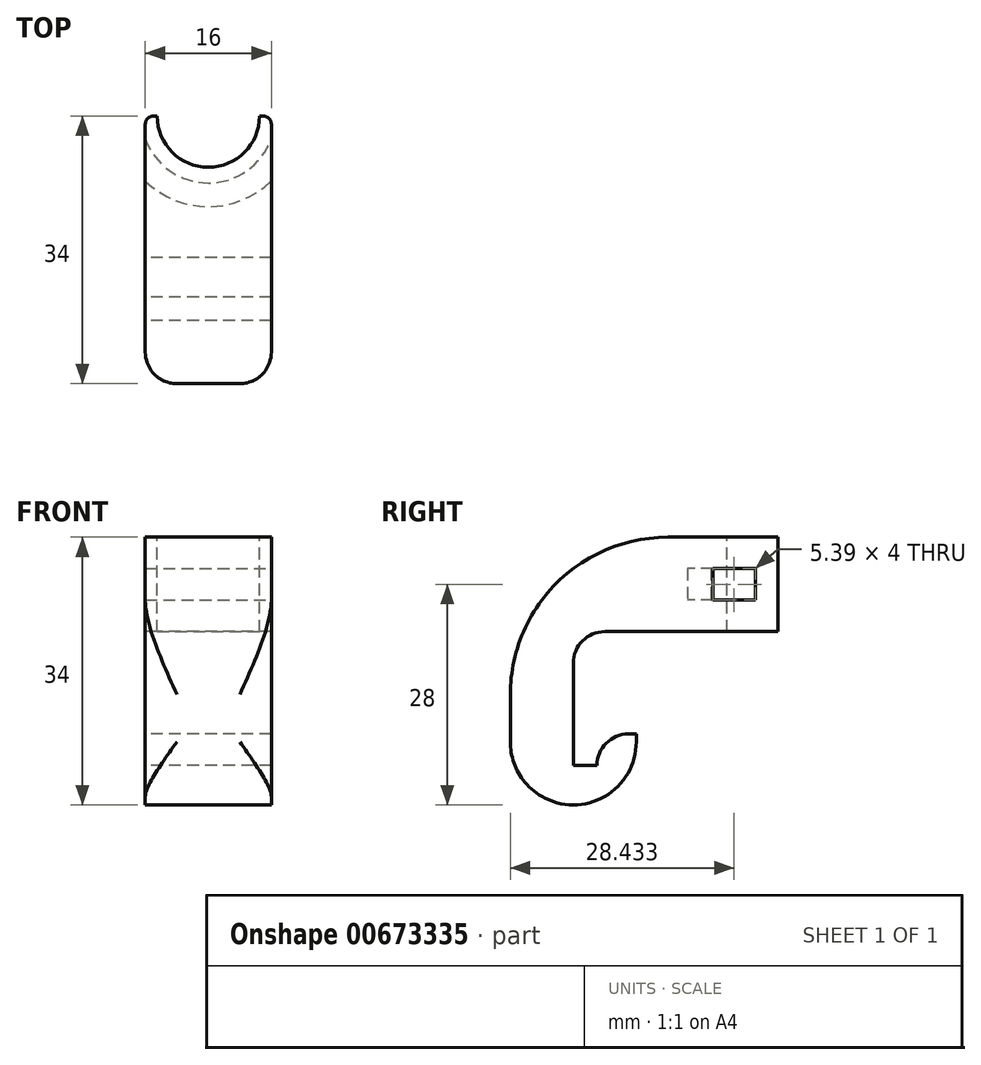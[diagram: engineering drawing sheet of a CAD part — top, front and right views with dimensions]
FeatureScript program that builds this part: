
annotation { "Feature Type Name" : "Feature", "Feature Type Description" : "" }
export const myFeature = defineFeature(function(context is Context, id is Id, definition is map)
    precondition{}
    {
        {
            var Q0;
            Q0=qCreatedBy(makeId("Right.planeOp"),FACE);
            var sketch = newSketch(context, id + "F0", { "sketchPlane" : qUnion([Q0])});
            skLineSegment(sketch, "E0", {"start": v(0, 34) * mm, "end": v(0, 0) * mm});
            skLineSegment(sketch, "E1", {"start": v(0, 0) * mm, "end": v(16, 0) * mm});
            skLineSegment(sketch, "E2", {"start": v(16, 0) * mm, "end": v(16, 9) * mm});
            skLineSegment(sketch, "E3", {"start": v(16, 9) * mm, "end": v(11, 9) * mm});
            skLineSegment(sketch, "E4", {"start": v(11, 9) * mm, "end": v(11, 5) * mm});
            skLineSegment(sketch, "E5", {"start": v(11, 5) * mm, "end": v(8, 5) * mm});
            skLineSegment(sketch, "E6", {"start": v(8, 5) * mm, "end": v(8, 22) * mm});
            skLineSegment(sketch, "E7", {"start": v(8, 22) * mm, "end": v(34, 22) * mm});
            skLineSegment(sketch, "E8", {"start": v(34, 22) * mm, "end": v(34, 34) * mm});
            skLineSegment(sketch, "E9", {"start": v(34, 34) * mm, "end": v(0, 34) * mm});
            skSolve(sketch);
        }
        {
            var Q0;
            Q0=makeQuery(id+"F0.imprint","IMPRINT",FACE,{"disambiguationData":[TD([[makeQuery(id+"F0.imprint","IMPRINT",EDGE,{"derivedFrom":sQuery(id+"F0.wireOp",EDGE,"E0")}),1.0]])]});
            extrude(context, id + "F1", {"entities" : qUnion([Q0]), "depth" : 16 * mm, "offsetDistance" : 25 * mm});
        }
        {
            var Q0;
            Q0=makeQuery(id+"F1.opExtrude","SWEPT_EDGE",EDGE,{"disambiguationData":[OSD([sQuery(id+"F0.wireOp",EDGE,"E1"),sQuery(id+"F0.wireOp",EDGE,"E2")])]});
            var Q1;
            Q1=makeQuery(id+"F1.opExtrude","SWEPT_EDGE",EDGE,{"disambiguationData":[OSD([sQuery(id+"F0.wireOp",EDGE,"E0"),sQuery(id+"F0.wireOp",EDGE,"E1")])]});
            fillet(context, id + "F2", {"entities" : qUnion([Q0, Q1]), "radius" : 8 * mm, "tangentPropagation" : true, "allowEdgeOverflow" : false});
        }
        {
            var Q0;
            Q0=makeQuery(id+"F1.opExtrude","SWEPT_EDGE",EDGE,{"disambiguationData":[OSD([sQuery(id+"F0.wireOp",EDGE,"E0"),sQuery(id+"F0.wireOp",EDGE,"E9")])]});
            fillet(context, id + "F3", {"entities" : qUnion([Q0]), "radius" : 20 * mm, "tangentPropagation" : true, "allowEdgeOverflow" : false});
        }
        {
            var Q0;
            Q0=makeQuery(id+"F1.opExtrude","SWEPT_EDGE",EDGE,{"disambiguationData":[OSD([sQuery(id+"F0.wireOp",EDGE,"E6"),sQuery(id+"F0.wireOp",EDGE,"E7")])]});
            var Q1;
            Q1=makeQuery(id+"F1.opExtrude","SWEPT_EDGE",EDGE,{"disambiguationData":[OSD([sQuery(id+"F0.wireOp",EDGE,"E3"),sQuery(id+"F0.wireOp",EDGE,"E4")])]});
            fillet(context, id + "F4", {"entities" : qUnion([Q0, Q1]), "radius" : 4 * mm, "tangentPropagation" : true, "allowEdgeOverflow" : false});
        }
        {
            var Q0;
            Q0=makeQuery(id+"F1.opExtrude","SWEPT_FACE",FACE,{"disambiguationData":[OSD([sQuery(id+"F0.wireOp",EDGE,"E9")])]});
            var sketch = newSketch(context, id + "F5", { "sketchPlane" : qUnion([Q0])});
            skCircle(sketch, "E10", {"center": v(8, 34) * mm, "radius": 6.5 * mm});
            skSolve(sketch);
        }
        {
            var Q0;
            {var subQ0=sQuery(id+"F5.wireOp",EDGE,"E10");var subQ1=makeQuery(id+"F1.opExtrude","SWEPT_EDGE",EDGE,{"disambiguationData":[OSD([sQuery(id+"F0.wireOp",EDGE,"E8"),sQuery(id+"F0.wireOp",EDGE,"E9")])]});var subQ2=makeQuery(id+"F5.imprint","INTERSECT",VERTEX,{"disambiguationData":[OD(0.0)],"derivedFrom":[subQ1,subQ0]});Q0=makeQuery(id+"F5.imprint","IMPRINT",FACE,{"disambiguationData":[TD([[makeQuery(id+"F5.imprint","IMPRINT",EDGE,{"disambiguationData":[TD([[subQ2,-1.0]])],"derivedFrom":subQ0}),1.0]])]});}
            extrude(context, id + "F6", {"entities" : qUnion([Q0]), "operationType" : NewBodyOperationType.REMOVE, "endBound" : BoundingType.THROUGH_ALL, "oppositeDirection" : true, "depth" : 25 * mm, "offsetDistance" : 25 * mm});
        }
        {
            var Q0;
            Q0=makeQuery(id+"F1.opExtrude","SWEPT_FACE",FACE,{"disambiguationData":[OSD([sQuery(id+"F0.wireOp",EDGE,"E9")])]});
            var sketch = newSketch(context, id + "F7", { "sketchPlane" : qUnion([Q0])});
            skCircle(sketch, "E11", {"center": v(8, 34) * mm, "radius": 8.5 * mm});
            skCircle(sketch, "E12", {"center": v(8, 34) * mm, "radius": 11.5 * mm});
            skSolve(sketch);
        }
        {
            var Q0;
            {var subQ1=sQuery(id+"F0.wireOp",EDGE,"E9");var subQ15=makeQuery(id+"F1.opExtrude","CAP_EDGE",EDGE,{"disambiguationData":[OSD([subQ1])],"isStart":true});var subQ19=sQuery(id+"F7.wireOp",EDGE,"E12");var subQ21=makeQuery(id+"F7.imprint","INTERSECT",VERTEX,{"derivedFrom":[subQ15,subQ19]});Q0=makeQuery(id+"F7.imprint","IMPRINT",FACE,{"disambiguationData":[TD([[makeQuery(id+"F7.imprint","IMPRINT",EDGE,{"disambiguationData":[TD([[subQ21,-1.0]])],"derivedFrom":subQ19}),1.0]])]});}
            extrude(context, id + "F8", {"entities" : qUnion([Q0]), "depth" : 4 * mm, "offsetDistance" : 25 * mm});
        }
        {
            var Q0;
            Q0=makeQuery(id+"F8.opExtrude","SWEPT_BODY",BODY,{"disambiguationData":[OSD([sQuery(id+"F0.wireOp",EDGE,"E9"),sQuery(id+"F7.wireOp",EDGE,"E11"),sQuery(id+"F7.wireOp",EDGE,"E12")])]});
            transform(context, id + "F9", {"entities" : qUnion([Q0]), "transformType" : TransformType.TRANSLATION_3D, "dx" : 0 * mm, "dy" : 0 * mm, "dz" : -8 * mm, "makeCopy" : false});
        }
        {
            var Q0;
            Q0=makeQuery(id+"F8.opExtrude","SWEPT_BODY",BODY,{"disambiguationData":[OSD([sQuery(id+"F0.wireOp",EDGE,"E9"),sQuery(id+"F7.wireOp",EDGE,"E11"),sQuery(id+"F7.wireOp",EDGE,"E12")])]});
            var Q1;
            Q1=makeQuery(id+"F1.opExtrude","SWEPT_BODY",BODY,{"disambiguationData":[OSD([sQuery(id+"F0.wireOp",EDGE,"E0"),sQuery(id+"F0.wireOp",EDGE,"E1"),sQuery(id+"F0.wireOp",EDGE,"E2"),sQuery(id+"F0.wireOp",EDGE,"E3"),sQuery(id+"F0.wireOp",EDGE,"E4"),sQuery(id+"F0.wireOp",EDGE,"E5"),sQuery(id+"F0.wireOp",EDGE,"E6"),sQuery(id+"F0.wireOp",EDGE,"E7"),sQuery(id+"F0.wireOp",EDGE,"E8"),sQuery(id+"F0.wireOp",EDGE,"E9")])]});
            booleanBodies(context, id + "F10", {"operationType" : BooleanOperationType.SUBTRACTION, "tools" : qUnion([Q0]), "targets" : qUnion([Q1])});
        }
        {
            var Q0;
            {var subQ0=sQuery(id+"F7.wireOp",EDGE,"E11");var subQ1=sQuery(id+"F0.wireOp",EDGE,"E9");var subQ2=sQuery(id+"F0.wireOp",EDGE,"E8");Q0=makeQuery(id+"F10.opBoolean","MERGE",EDGE,{"derivedFrom":[makeQuery(id+"F1.opExtrude","CAP_EDGE",EDGE,{"disambiguationData":[OSD([subQ2])],"isStart":false}),makeQuery(id+"F8.opExtrude","SWEPT_EDGE",EDGE,{"disambiguationData":[OSD([subQ2,subQ1,subQ0]),TDD([makeQuery(id+"F7.imprint","INTERSECT",VERTEX,{"derivedFrom":[makeQuery(id+"F1.opExtrude","CAP_EDGE",EDGE,{"disambiguationData":[OSD([subQ1])],"isStart":false}),makeQuery(id+"F6.boolean.opBoolean","SPLIT",EDGE,{"disambiguationData":[TD([makeQuery(id+"F1.opExtrude","CAP_FACE",FACE,{"disambiguationData":[OSD([sQuery(id+"F0.wireOp",EDGE,"E0"),sQuery(id+"F0.wireOp",EDGE,"E1"),sQuery(id+"F0.wireOp",EDGE,"E2"),sQuery(id+"F0.wireOp",EDGE,"E3"),sQuery(id+"F0.wireOp",EDGE,"E4"),sQuery(id+"F0.wireOp",EDGE,"E5"),sQuery(id+"F0.wireOp",EDGE,"E6"),sQuery(id+"F0.wireOp",EDGE,"E7"),subQ2,subQ1])],"isStart":false})])],"derivedFrom":makeQuery(id+"F1.opExtrude","SWEPT_EDGE",EDGE,{"disambiguationData":[OSD([subQ2,subQ1])]})}),subQ0]})])]})]});}
            var Q1;
            {var subQ0=sQuery(id+"F7.wireOp",EDGE,"E12");var subQ1=sQuery(id+"F0.wireOp",EDGE,"E9");Q1=makeQuery(id+"F10.opBoolean","COPY",EDGE,{"derivedFrom":makeQuery(id+"F8.opExtrude","SWEPT_EDGE",EDGE,{"disambiguationData":[OSD([subQ1,subQ0]),TDD([makeQuery(id+"F7.imprint","INTERSECT",VERTEX,{"derivedFrom":[makeQuery(id+"F1.opExtrude","CAP_EDGE",EDGE,{"disambiguationData":[OSD([subQ1])],"isStart":false}),subQ0]})])]})});}
            var Q2;
            {var subQ0=sQuery(id+"F7.wireOp",EDGE,"E11");var subQ1=sQuery(id+"F0.wireOp",EDGE,"E9");var subQ2=sQuery(id+"F0.wireOp",EDGE,"E8");Q2=makeQuery(id+"F10.opBoolean","MERGE",EDGE,{"derivedFrom":[makeQuery(id+"F1.opExtrude","CAP_EDGE",EDGE,{"disambiguationData":[OSD([subQ2])],"isStart":true}),makeQuery(id+"F8.opExtrude","SWEPT_EDGE",EDGE,{"disambiguationData":[OSD([subQ2,subQ1,subQ0]),TDD([makeQuery(id+"F7.imprint","INTERSECT",VERTEX,{"derivedFrom":[makeQuery(id+"F1.opExtrude","CAP_EDGE",EDGE,{"disambiguationData":[OSD([subQ1])],"isStart":true}),makeQuery(id+"F6.boolean.opBoolean","SPLIT",EDGE,{"disambiguationData":[TD([makeQuery(id+"F1.opExtrude","CAP_FACE",FACE,{"disambiguationData":[OSD([sQuery(id+"F0.wireOp",EDGE,"E0"),sQuery(id+"F0.wireOp",EDGE,"E1"),sQuery(id+"F0.wireOp",EDGE,"E2"),sQuery(id+"F0.wireOp",EDGE,"E3"),sQuery(id+"F0.wireOp",EDGE,"E4"),sQuery(id+"F0.wireOp",EDGE,"E5"),sQuery(id+"F0.wireOp",EDGE,"E6"),sQuery(id+"F0.wireOp",EDGE,"E7"),subQ2,subQ1])],"isStart":true})])],"derivedFrom":makeQuery(id+"F1.opExtrude","SWEPT_EDGE",EDGE,{"disambiguationData":[OSD([subQ2,subQ1])]})}),subQ0]})])]})]});}
            var Q3;
            {var subQ0=sQuery(id+"F7.wireOp",EDGE,"E12");var subQ1=sQuery(id+"F0.wireOp",EDGE,"E9");Q3=makeQuery(id+"F10.opBoolean","COPY",EDGE,{"derivedFrom":makeQuery(id+"F8.opExtrude","SWEPT_EDGE",EDGE,{"disambiguationData":[OSD([subQ1,subQ0]),TDD([makeQuery(id+"F7.imprint","INTERSECT",VERTEX,{"derivedFrom":[makeQuery(id+"F1.opExtrude","CAP_EDGE",EDGE,{"disambiguationData":[OSD([subQ1])],"isStart":true}),subQ0]})])]})});}
            fillet(context, id + "F11", {"entities" : qUnion([Q0, Q1, Q2, Q3]), "radius" : 1 * mm, "tangentPropagation" : true, "allowEdgeOverflow" : false});
        }
        {
            var Q0;
            Q0=makeQuery(id+"F1.opExtrude","CAP_EDGE",EDGE,{"disambiguationData":[OSD([sQuery(id+"F0.wireOp",EDGE,"E0")])],"isStart":false});
            var Q1;
            Q1=makeQuery(id+"F1.opExtrude","CAP_EDGE",EDGE,{"disambiguationData":[OSD([sQuery(id+"F0.wireOp",EDGE,"E0")])],"isStart":true});
            fillet(context, id + "F12", {"entities" : qUnion([Q0, Q1]), "radius" : 4 * mm, "allowEdgeOverflow" : false});
        }
    });
